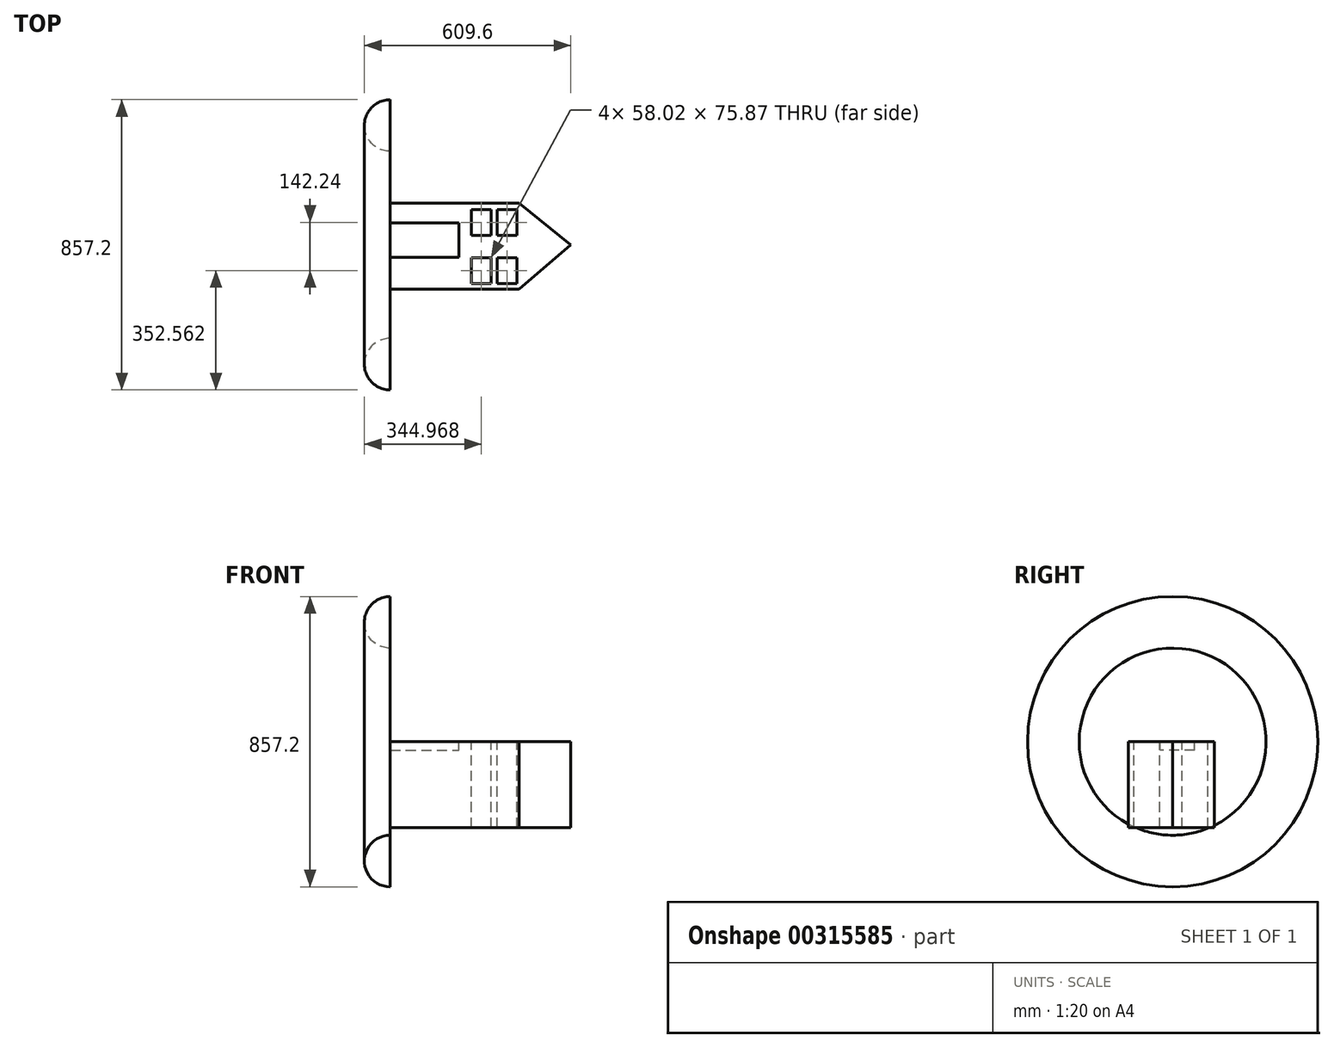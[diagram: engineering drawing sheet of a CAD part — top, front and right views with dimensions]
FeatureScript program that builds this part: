
annotation { "Feature Type Name" : "Feature", "Feature Type Description" : "" }
export const myFeature = defineFeature(function(context is Context, id is Id, definition is map)
    precondition{}
    {
        {
            var Q0;
            Q0=qCreatedBy(makeId("Top.planeOp"),FACE);
            var sketch = newSketch(context, id + "F0", { "sketchPlane" : qUnion([Q0])});
            skLineSegment(sketch, "E0.bottom", {"start": v(111.1, 123.4) * mm, "end": v(-269.9, 123.4) * mm});
            skLineSegment(sketch, "E0.top", {"start": v(111.1, -130.6) * mm, "end": v(-269.9, -130.6) * mm});
            skLineSegment(sketch, "E0.left", {"start": v(111.1, 123.4) * mm, "end": v(111.1, -130.6) * mm});
            skLineSegment(sketch, "E0.right", {"start": v(-269.9, 123.4) * mm, "end": v(-269.9, -130.6) * mm});
            skPoint(sketch, "E1.middle", {"position": v(0, 0) * mm});
            skLineSegment(sketch, "E2", {"start": v(111.1, 123.4) * mm, "end": v(263.5, 0) * mm});
            skLineSegment(sketch, "E3", {"start": v(263.5, 0) * mm, "end": v(111.1, -130.6) * mm});
            skSolve(sketch);
        }
        {
            var Q0;
            Q0=makeQuery(id+"F0.imprint","IMPRINT",FACE,{"disambiguationData":[TD([[makeQuery(id+"F0.imprint","IMPRINT",EDGE,{"derivedFrom":sQuery(id+"F0.wireOp",EDGE,"E0.bottom")}),1.0]])]});
            var Q1;
            Q1=makeQuery(id+"F0.imprint","IMPRINT",FACE,{"disambiguationData":[TD([[makeQuery(id+"F0.imprint","IMPRINT",EDGE,{"derivedFrom":sQuery(id+"F0.wireOp",EDGE,"E0.left")}),1.0]])]});
            extrude(context, id + "F1", {"entities" : qUnion([Q0, Q1]), "depth" : 254 * mm});
        }
        {
            var Q0;
            Q0=makeQuery(id+"F1.opExtrude","CAP_FACE",FACE,{"disambiguationData":[OSD([sQuery(id+"F0.wireOp",EDGE,"E0.bottom"),sQuery(id+"F0.wireOp",EDGE,"E0.top"),sQuery(id+"F0.wireOp",EDGE,"E0.right"),sQuery(id+"F0.wireOp",EDGE,"E2"),sQuery(id+"F0.wireOp",EDGE,"E3")])],"isStart":false});
            var sketch = newSketch(context, id + "F2", { "sketchPlane" : qUnion([Q0])});
            skSolve(sketch);
        }
        {
            var Q0;
            Q0=makeQuery(id+"F2.imprint","IMPRINT",FACE,{"disambiguationData":[TD([[makeQuery(id+"F2.imprint","IMPRINT",EDGE,{"derivedFrom":makeQuery(id+"F1.opExtrude","CAP_EDGE",EDGE,{"disambiguationData":[OSD([sQuery(id+"F0.wireOp",EDGE,"E0.bottom")])],"isStart":false})}),1.0]])]});
            var sketch = newSketch(context, id + "F3", { "sketchPlane" : qUnion([Q0])});
            skLineSegment(sketch, "E4", {"start": v(111.1, -130.6) * mm, "end": v(-269.9, -130.6) * mm});
            skLineSegment(sketch, "E5", {"start": v(263.5, 0) * mm, "end": v(111.1, -130.6) * mm});
            skLineSegment(sketch, "E6", {"start": v(111.1, 123.4) * mm, "end": v(263.5, 0) * mm});
            skLineSegment(sketch, "E7", {"start": v(111.1, 123.4) * mm, "end": v(-269.9, 123.4) * mm});
            skLineSegment(sketch, "E8", {"start": v(-269.9, 123.4) * mm, "end": v(-269.9, -130.6) * mm});
            skLineSegment(sketch, "E9.bottom", {"start": v(-269.9, 65.18) * mm, "end": v(-66.7, 65.18) * mm});
            skLineSegment(sketch, "E9.top", {"start": v(-269.9, -36.42) * mm, "end": v(-66.7, -36.42) * mm});
            skLineSegment(sketch, "E9.left", {"start": v(-269.9, 65.18) * mm, "end": v(-269.9, -36.42) * mm});
            skLineSegment(sketch, "E9.right", {"start": v(-66.7, 65.18) * mm, "end": v(-66.7, -36.42) * mm});
            skSolve(sketch);
        }
        {
            var Q0;
            Q0=makeQuery(id+"F3.imprint","IMPRINT",FACE,{"disambiguationData":[TD([[makeQuery(id+"F3.imprint","IMPRINT",EDGE,{"derivedFrom":sQuery(id+"F3.wireOp",EDGE,"E9.bottom")}),-1.0]])]});
            extrude(context, id + "F4", {"entities" : qUnion([Q0]), "operationType" : NewBodyOperationType.REMOVE, "oppositeDirection" : true, "depth" : 25.4 * mm});
        }
        {
            var Q0;
            Q0=makeQuery(id+"F2.imprint","IMPRINT",FACE,{"disambiguationData":[TD([[makeQuery(id+"F2.imprint","IMPRINT",EDGE,{"derivedFrom":makeQuery(id+"F1.opExtrude","CAP_EDGE",EDGE,{"disambiguationData":[OSD([sQuery(id+"F0.wireOp",EDGE,"E0.bottom")])],"isStart":false})}),1.0]])]});
            var sketch = newSketch(context, id + "F5", { "sketchPlane" : qUnion([Q0])});
            skLineSegment(sketch, "E10.0.0", {"start": v(-269.9, -130.6) * mm, "end": v(111.1, -130.6) * mm});
            skLineSegment(sketch, "E10.0.1", {"start": v(111.1, -130.6) * mm, "end": v(263.5, 0) * mm});
            skLineSegment(sketch, "E10.0.2", {"start": v(263.5, 0) * mm, "end": v(111.1, 123.4) * mm});
            skLineSegment(sketch, "E10.0.3", {"start": v(111.1, 123.4) * mm, "end": v(-269.9, 123.4) * mm});
            skLineSegment(sketch, "E10.0.4", {"start": v(-269.9, 123.4) * mm, "end": v(-269.9, -130.6) * mm});
            skArc(sketch, "E11", {"start": v(-269.9, 428.6) * mm, "mid": v(-346.1, 352.4) * mm, "end": v(-269.9, 276.2) * mm});
            skLineSegment(sketch, "E12", {"start": v(-269.9, 428.6) * mm, "end": v(-269.9, 276.2) * mm});
            skLineSegment(sketch, "E13", {"start": v(263.5, 0) * mm, "end": v(-269.9, 0) * mm, "construction": true});
            skSolve(sketch);
        }
        {
            var Q0;
            Q0=makeQuery(id+"F5.imprint","IMPRINT",FACE,{"disambiguationData":[TD([[makeQuery(id+"F5.imprint","IMPRINT",EDGE,{"derivedFrom":sQuery(id+"F5.wireOp",EDGE,"E11")}),1.0]])]});
            var Q1;
            Q1=sQuery(id+"F5.wireOp",EDGE,"E13");
            revolve(context, id + "F6", {"operationType" : NewBodyOperationType.ADD, "entities" : qUnion([Q0]), "axis" : qUnion([Q1]), "revolveType" : RevolveType.FULL});
        }
        {
            var Q0;
            Q0=makeQuery(id+"F2.imprint","IMPRINT",FACE,{"disambiguationData":[TD([[makeQuery(id+"F2.imprint","IMPRINT",EDGE,{"derivedFrom":makeQuery(id+"F1.opExtrude","CAP_EDGE",EDGE,{"disambiguationData":[OSD([sQuery(id+"F0.wireOp",EDGE,"E0.bottom")])],"isStart":false})}),1.0]])]});
            var sketch = newSketch(context, id + "F7", { "sketchPlane" : qUnion([Q0])});
            skLineSegment(sketch, "E14.bottom", {"start": v(27.88, 104.14) * mm, "end": v(-30.14, 104.14) * mm});
            skLineSegment(sketch, "E14.top", {"start": v(27.88, 28.27) * mm, "end": v(-30.14, 28.27) * mm});
            skLineSegment(sketch, "E14.left", {"start": v(27.88, 104.14) * mm, "end": v(27.88, 28.27) * mm});
            skLineSegment(sketch, "E14.right", {"start": v(-30.14, 104.14) * mm, "end": v(-30.14, 28.27) * mm});
            skLineSegment(sketch, "E15.0.1.0", {"start": v(27.88, -38.1) * mm, "end": v(27.88, -113.97) * mm});
            skLineSegment(sketch, "E15.0.1.1", {"start": v(27.88, -113.97) * mm, "end": v(-30.14, -113.97) * mm});
            skLineSegment(sketch, "E15.0.1.2", {"start": v(-30.14, -38.1) * mm, "end": v(-30.14, -113.97) * mm});
            skLineSegment(sketch, "E15.0.1.3", {"start": v(27.88, -38.1) * mm, "end": v(-30.14, -38.1) * mm});
            skLineSegment(sketch, "E15.1.0.0", {"start": v(104.08, 104.14) * mm, "end": v(104.08, 28.27) * mm});
            skLineSegment(sketch, "E15.1.0.1", {"start": v(104.08, 28.27) * mm, "end": v(46.06, 28.27) * mm});
            skLineSegment(sketch, "E15.1.0.2", {"start": v(46.06, 104.14) * mm, "end": v(46.06, 28.27) * mm});
            skLineSegment(sketch, "E15.1.0.3", {"start": v(104.08, 104.14) * mm, "end": v(46.06, 104.14) * mm});
            skLineSegment(sketch, "E15.1.1.0", {"start": v(104.08, -38.1) * mm, "end": v(104.08, -113.97) * mm});
            skLineSegment(sketch, "E15.1.1.1", {"start": v(104.08, -113.97) * mm, "end": v(46.06, -113.97) * mm});
            skLineSegment(sketch, "E15.1.1.2", {"start": v(46.06, -38.1) * mm, "end": v(46.06, -113.97) * mm});
            skLineSegment(sketch, "E15.1.1.3", {"start": v(104.08, -38.1) * mm, "end": v(46.06, -38.1) * mm});
            skLineSegment(sketch, "E15.direction1", {"start": v(27.88, 28.27) * mm, "end": v(104.08, 28.27) * mm, "construction": true});
            skLineSegment(sketch, "E15.direction2", {"start": v(27.88, 28.27) * mm, "end": v(27.88, -113.97) * mm, "construction": true});
            skSolve(sketch);
        }
        {
            var Q0;
            Q0=makeQuery(id+"F7.imprint","IMPRINT",FACE,{"disambiguationData":[TD([[makeQuery(id+"F7.imprint","IMPRINT",EDGE,{"derivedFrom":sQuery(id+"F7.wireOp",EDGE,"E15.1.0.0")}),-1.0]])]});
            var Q1;
            Q1=makeQuery(id+"F7.imprint","IMPRINT",FACE,{"disambiguationData":[TD([[makeQuery(id+"F7.imprint","IMPRINT",EDGE,{"derivedFrom":sQuery(id+"F7.wireOp",EDGE,"E14.bottom")}),1.0]])]});
            var Q2;
            Q2=makeQuery(id+"F7.imprint","IMPRINT",FACE,{"disambiguationData":[TD([[makeQuery(id+"F7.imprint","IMPRINT",EDGE,{"derivedFrom":sQuery(id+"F7.wireOp",EDGE,"E15.0.1.0")}),-1.0]])]});
            var Q3;
            Q3=makeQuery(id+"F7.imprint","IMPRINT",FACE,{"disambiguationData":[TD([[makeQuery(id+"F7.imprint","IMPRINT",EDGE,{"derivedFrom":sQuery(id+"F7.wireOp",EDGE,"E15.1.1.0")}),-1.0]])]});
            var Q4;
            Q4=makeQuery(id+"F1.opExtrude","CAP_FACE",FACE,{"disambiguationData":[OSD([sQuery(id+"F0.wireOp",EDGE,"E0.bottom"),sQuery(id+"F0.wireOp",EDGE,"E0.top"),sQuery(id+"F0.wireOp",EDGE,"E0.right"),sQuery(id+"F0.wireOp",EDGE,"E2"),sQuery(id+"F0.wireOp",EDGE,"E3")])],"isStart":true});
            extrude(context, id + "F8", {"entities" : qUnion([Q0, Q1, Q2, Q3]), "operationType" : NewBodyOperationType.REMOVE, "endBound" : BoundingType.UP_TO_SURFACE, "oppositeDirection" : true, "endBoundEntityFace" : qUnion([Q4]), "depth" : 25.4 * mm});
        }
    });
